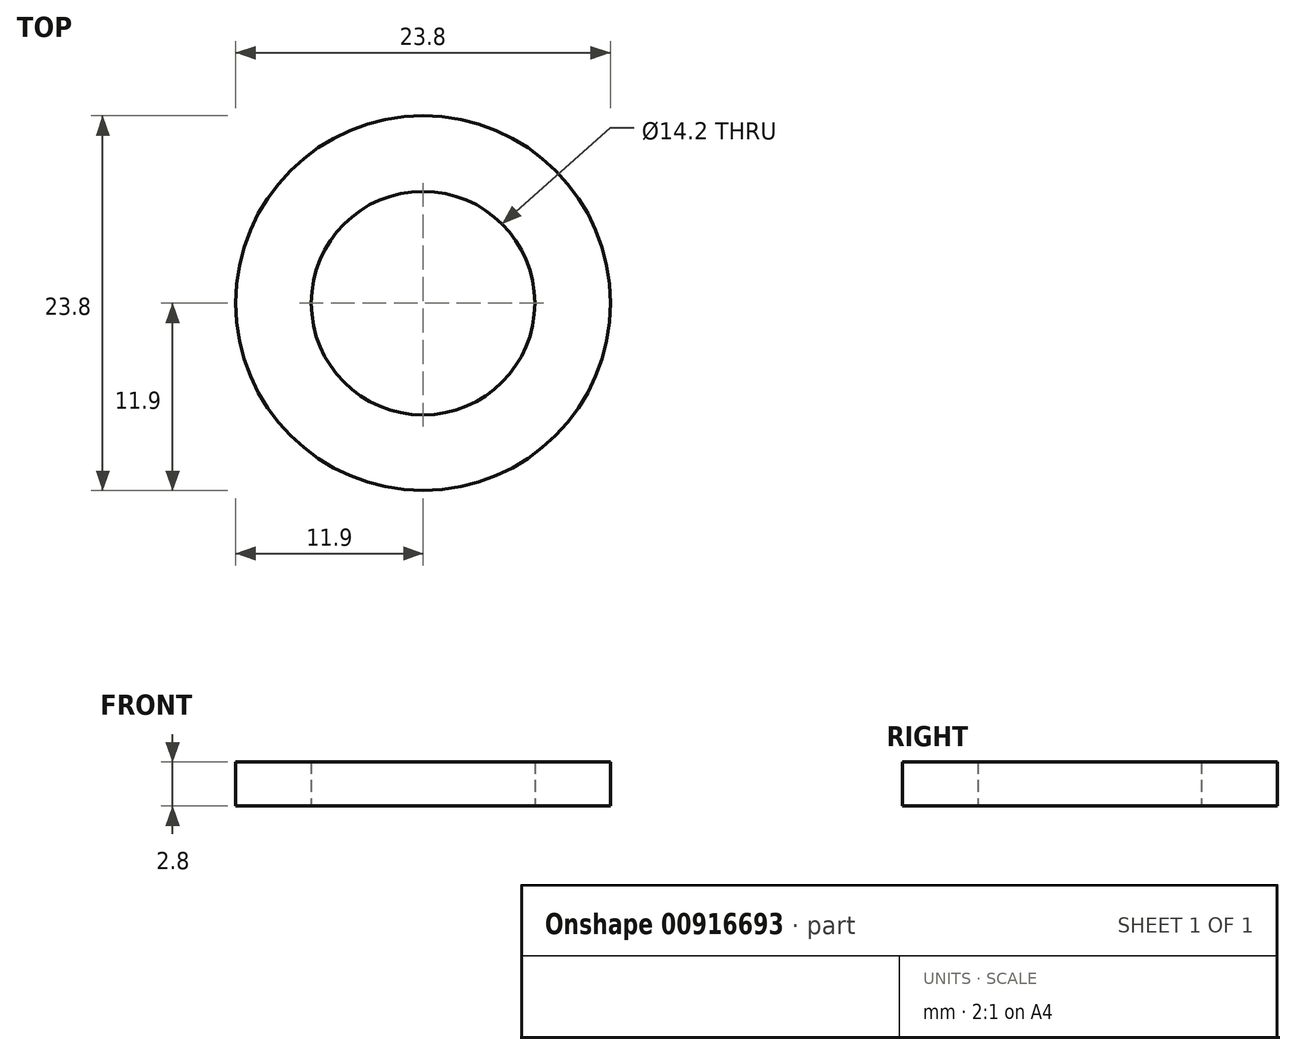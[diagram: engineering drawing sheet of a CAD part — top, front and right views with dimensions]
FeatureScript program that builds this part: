
annotation { "Feature Type Name" : "Feature", "Feature Type Description" : "" }
export const myFeature = defineFeature(function(context is Context, id is Id, definition is map)
    precondition{}
    {
        {
            var Q0;
            Q0=qCreatedBy(makeId("Top.planeOp"),FACE);
            var sketch = newSketch(context, id + "F0", { "sketchPlane" : qUnion([Q0])});
            skCircle(sketch, "E0", {"center": v(0, 0) * mm, "radius": 7.1 * mm});
            skCircle(sketch, "E1", {"center": v(0, 0) * mm, "radius": 11.9 * mm});
            skSolve(sketch);
        }
        {
            var Q0;
            Q0 = qSketchRegion(id + "F0", true);
            extrude(context, id + "F1", {"entities" : qUnion([Q0]), "depth" : 2.8 * mm, "offsetDistance" : 25 * mm});
        }
    });
